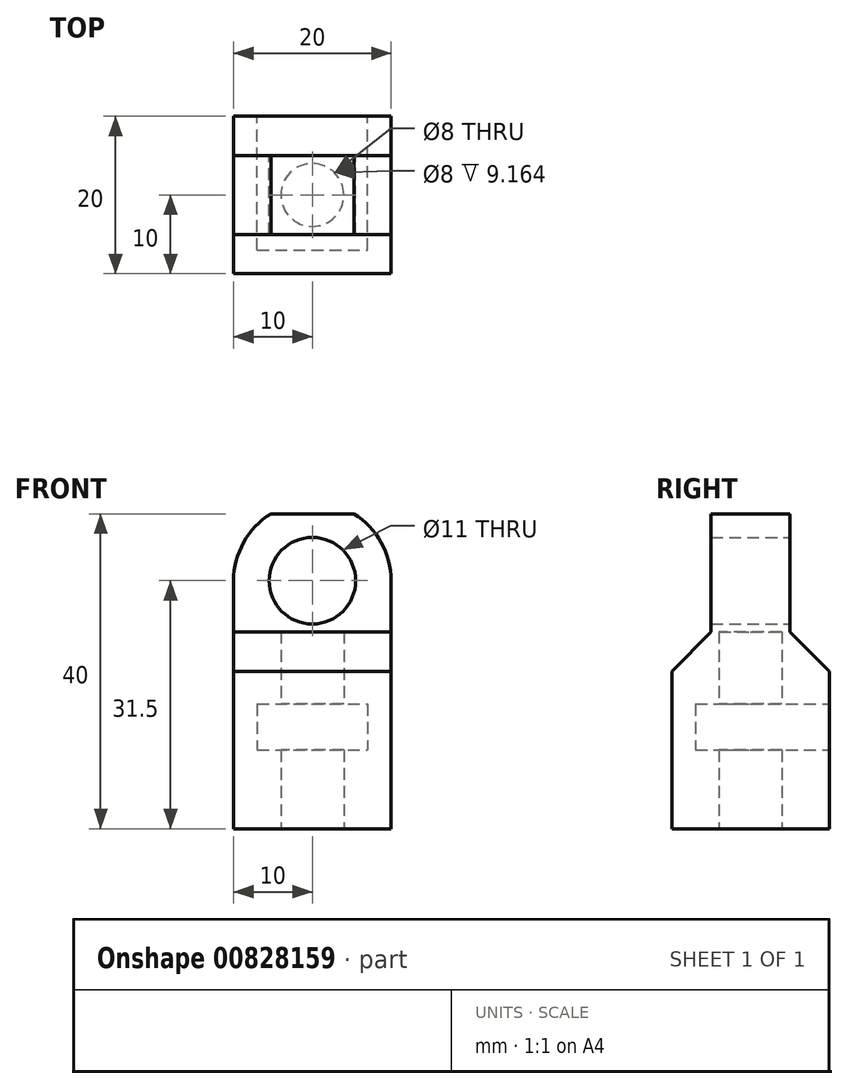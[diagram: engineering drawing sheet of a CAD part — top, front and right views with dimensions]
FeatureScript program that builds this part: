
annotation { "Feature Type Name" : "Feature", "Feature Type Description" : "" }
export const myFeature = defineFeature(function(context is Context, id is Id, definition is map)
    precondition{}
    {
        {
            var Q0;
            Q0=qCreatedBy(makeId("Top.planeOp"),FACE);
            var sketch = newSketch(context, id + "F0", { "sketchPlane" : qUnion([Q0])});
            skLineSegment(sketch, "E0.bottom", {"start": v(10, 10) * mm, "end": v(-10, 10) * mm});
            skLineSegment(sketch, "E0.top", {"start": v(10, -10) * mm, "end": v(-10, -10) * mm});
            skLineSegment(sketch, "E0.left", {"start": v(10, 10) * mm, "end": v(10, -10) * mm});
            skLineSegment(sketch, "E0.right", {"start": v(-10, 10) * mm, "end": v(-10, -10) * mm});
            skPoint(sketch, "E0.middle", {"position": v(0, 0) * mm});
            skCircle(sketch, "E1", {"center": v(0, 0) * mm, "radius": 4 * mm});
            skSolve(sketch);
        }
        {
            var Q0;
            Q0=makeQuery(id+"F0.imprint","IMPRINT",FACE,{"disambiguationData":[TD([[makeQuery(id+"F0.imprint","IMPRINT",EDGE,{"derivedFrom":sQuery(id+"F0.wireOp",EDGE,"E0.bottom")}),1.0]])]});
            extrude(context, id + "F1", {"entities" : qUnion([Q0]), "depth" : 25 * mm, "offsetDistance" : 25 * mm});
        }
        {
            var Q0;
            Q0=makeQuery(id+"F1.opExtrude","SWEPT_FACE",FACE,{"disambiguationData":[OSD([sQuery(id+"F0.wireOp",EDGE,"E0.bottom")])]});
            cPlane(context, id + "F2", {"entities" : qUnion([Q0]), "cplaneType" : CPlaneType.OFFSET, "offset" : 0 * mm, "width" : 150 * mm, "height" : 150 * mm});
        }
        {
            var Q0;
            Q0=qCreatedBy(id+"F2.planeOp",FACE);
            var sketch = newSketch(context, id + "F3", { "sketchPlane" : qUnion([Q0])});
            skLineSegment(sketch, "E2.0", {"start": v(-10, 25) * mm, "end": v(-10, 0) * mm});
            skLineSegment(sketch, "E3.0", {"start": v(10, 25) * mm, "end": v(10, 0) * mm});
            skLineSegment(sketch, "E4.0", {"start": v(-10, 25) * mm, "end": v(10, 25) * mm});
            skLineSegment(sketch, "E5.bottom", {"start": v(7, 15.84) * mm, "end": v(-7, 15.84) * mm});
            skLineSegment(sketch, "E5.top", {"start": v(7, 10) * mm, "end": v(-7, 10) * mm});
            skLineSegment(sketch, "E5.left", {"start": v(7, 15.84) * mm, "end": v(7, 10) * mm});
            skLineSegment(sketch, "E5.right", {"start": v(-7, 15.84) * mm, "end": v(-7, 10) * mm});
            skPoint(sketch, "E5.middle", {"position": v(0, 12.92) * mm});
            skSolve(sketch);
        }
        {
            var Q0;
            Q0=makeQuery(id+"F3.imprint","IMPRINT",FACE,{"disambiguationData":[TD([[makeQuery(id+"F3.imprint","IMPRINT",EDGE,{"derivedFrom":sQuery(id+"F3.wireOp",EDGE,"E5.bottom")}),1.0]])]});
            extrude(context, id + "F4", {"entities" : qUnion([Q0]), "operationType" : NewBodyOperationType.REMOVE, "oppositeDirection" : true, "depth" : 17 * mm, "offsetDistance" : 25 * mm});
        }
        {
            var Q0;
            Q0=makeQuery(id+"F1.opExtrude","CAP_FACE",FACE,{"disambiguationData":[OSD([sQuery(id+"F0.wireOp",EDGE,"E0.bottom"),sQuery(id+"F0.wireOp",EDGE,"E0.top"),sQuery(id+"F0.wireOp",EDGE,"E0.left"),sQuery(id+"F0.wireOp",EDGE,"E0.right"),sQuery(id+"F0.wireOp",EDGE,"E1")])],"isStart":false});
            cPlane(context, id + "F5", {"entities" : qUnion([Q0]), "cplaneType" : CPlaneType.OFFSET, "offset" : 0 * mm, "width" : 150 * mm, "height" : 150 * mm});
        }
        {
            var Q0;
            Q0=qCreatedBy(id+"F5.planeOp",FACE);
            var sketch = newSketch(context, id + "F6", { "sketchPlane" : qUnion([Q0])});
            skLineSegment(sketch, "E6.bottom", {"start": v(10, 5) * mm, "end": v(-10, 5) * mm});
            skLineSegment(sketch, "E6.top", {"start": v(10, -5) * mm, "end": v(-10, -5) * mm});
            skLineSegment(sketch, "E6.left", {"start": v(10, 5) * mm, "end": v(10, -5) * mm});
            skLineSegment(sketch, "E6.right", {"start": v(-10, 5) * mm, "end": v(-10, -5) * mm});
            skPoint(sketch, "E6.middle", {"position": v(0, 0) * mm});
            skSolve(sketch);
        }
        {
            var Q0;
            Q0=makeQuery(id+"F6.imprint","IMPRINT",FACE,{"disambiguationData":[TD([[makeQuery(id+"F6.imprint","IMPRINT",EDGE,{"derivedFrom":sQuery(id+"F6.wireOp",EDGE,"E6.bottom")}),1.0]])]});
            extrude(context, id + "F7", {"entities" : qUnion([Q0]), "operationType" : NewBodyOperationType.ADD, "depth" : 15 * mm, "offsetDistance" : 25 * mm});
        }
        {
            var Q0;
            Q0=makeQuery(id+"F7.opExtrude","SWEPT_FACE",FACE,{"disambiguationData":[OSD([sQuery(id+"F6.wireOp",EDGE,"E6.bottom")])]});
            cPlane(context, id + "F8", {"entities" : qUnion([Q0]), "cplaneType" : CPlaneType.OFFSET, "offset" : 0 * mm, "width" : 150 * mm, "height" : 150 * mm});
        }
        {
            var Q0;
            Q0=qCreatedBy(id+"F8.planeOp",FACE);
            var sketch = newSketch(context, id + "F9", { "sketchPlane" : qUnion([Q0])});
            skLineSegment(sketch, "E7.0", {"start": v(-10, 40) * mm, "end": v(10, 40) * mm});
            skLineSegment(sketch, "E8.0", {"start": v(-10, 40) * mm, "end": v(-10, 25) * mm});
            skLineSegment(sketch, "E9.0", {"start": v(10, 40) * mm, "end": v(10, 25) * mm});
            skCircle(sketch, "E10", {"center": v(0, 31.5) * mm, "radius": 5.5 * mm});
            skCircle(sketch, "E11.0", {"center": v(0, 31.5) * mm, "radius": 10 * mm});
            skSolve(sketch);
        }
        {
            var Q0;
            {var subQ0=sQuery(id+"F9.wireOp",EDGE,"E8.0");var subQ1=sQuery(id+"F9.wireOp",EDGE,"E7.0");var subQ2=makeQuery(id+"F9.imprint","INTERSECT",VERTEX,{"derivedFrom":[subQ1,subQ0]});Q0=makeQuery(id+"F9.imprint","IMPRINT",FACE,{"disambiguationData":[TD([[makeQuery(id+"F9.imprint","IMPRINT",EDGE,{"disambiguationData":[TD([[subQ2,-1.0]])],"derivedFrom":subQ1}),-1.0]])]});}
            var Q1;
            {var subQ0=sQuery(id+"F9.wireOp",EDGE,"E9.0");var subQ1=sQuery(id+"F9.wireOp",EDGE,"E7.0");var subQ2=makeQuery(id+"F9.imprint","INTERSECT",VERTEX,{"derivedFrom":[subQ1,subQ0]});Q1=makeQuery(id+"F9.imprint","IMPRINT",FACE,{"disambiguationData":[TD([[makeQuery(id+"F9.imprint","IMPRINT",EDGE,{"disambiguationData":[TD([[subQ2,1.0]])],"derivedFrom":subQ1}),-1.0]])]});}
            extrude(context, id + "F10", {"entities" : qUnion([Q0, Q1]), "operationType" : NewBodyOperationType.REMOVE, "oppositeDirection" : true, "depth" : 10 * mm, "offsetDistance" : 25 * mm});
        }
        {
            var Q0;
            Q0=makeQuery(id+"F9.imprint","IMPRINT",FACE,{"disambiguationData":[TD([[makeQuery(id+"F9.imprint","IMPRINT",EDGE,{"derivedFrom":sQuery(id+"F9.wireOp",EDGE,"E10")}),1.0]])]});
            extrude(context, id + "F11", {"entities" : qUnion([Q0]), "operationType" : NewBodyOperationType.REMOVE, "oppositeDirection" : true, "depth" : 10 * mm, "offsetDistance" : 25 * mm});
        }
        {
            var Q0;
            Q0=makeQuery(id+"F1.opExtrude","CAP_EDGE",EDGE,{"disambiguationData":[OSD([sQuery(id+"F0.wireOp",EDGE,"E0.top")])],"isStart":false});
            var Q1;
            Q1=makeQuery(id+"F1.opExtrude","CAP_EDGE",EDGE,{"disambiguationData":[OSD([sQuery(id+"F0.wireOp",EDGE,"E0.bottom")])],"isStart":false});
            chamfer(context, id + "F12", {"entities" : qUnion([Q0, Q1]), "width" : 5 * mm, "tangentPropagation" : true});
        }
    });
